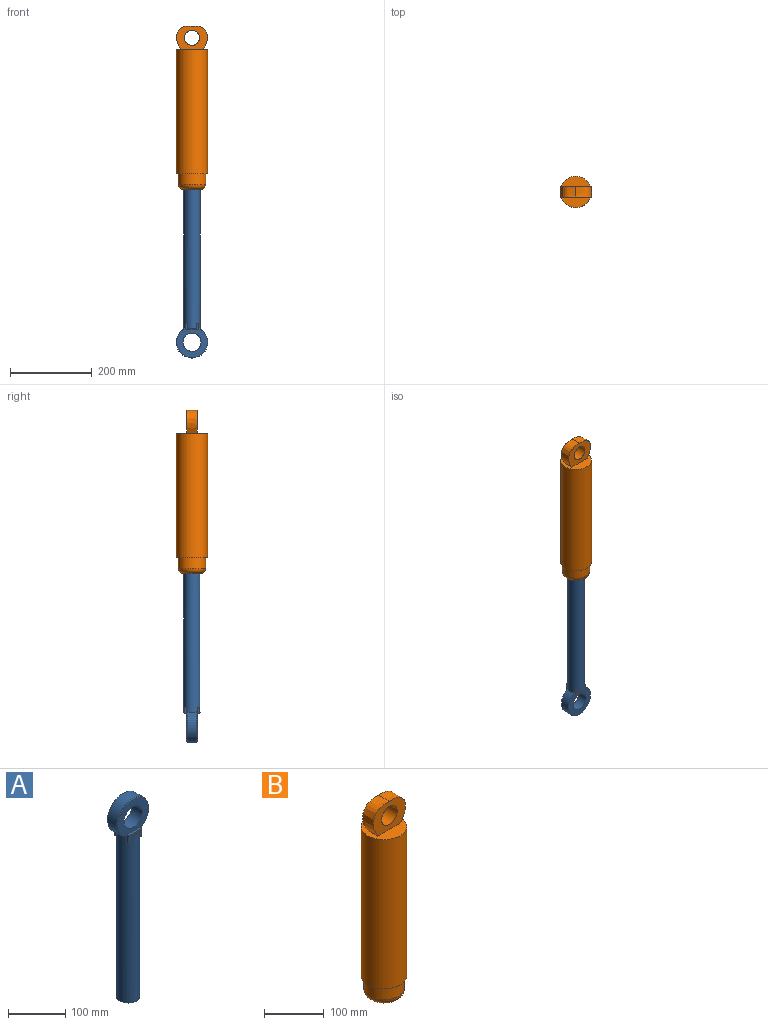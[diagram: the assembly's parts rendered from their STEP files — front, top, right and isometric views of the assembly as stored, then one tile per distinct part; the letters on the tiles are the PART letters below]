
ASSEMBLY  parts=2 mates=1
PART A: 24 faces, bbox 77.5x40.6x427.7 mm
  f0: cylinder r=20.32mm len=355.6mm, axis (0,0,-1), area 44958.8mm2, adj f1,f4,f5,f6,f7,f8,f10,f11
  f1: plane 19.87x2.59mm, normal (0,0,1), area 34.8mm2, adj f0,f17
  f2: plane 74.96x71.44mm, normal (0,1,0), area 2660.6mm2, adj f18,f19,f20,f21,f22
  f3: plane 74.96x71.44mm, normal (0,-1,0), area 2660.6mm2, adj f9,f10,f11,f21,f23
  f4: plane 9.02x0.51mm, normal (0,0,1), area 3.1mm2, adj f0,f8
  f5: plane 9.02x0.51mm, normal (0,0,1), area 3.1mm2, adj f0,f8
  f6: plane 19.87x2.59mm, normal (0,0,1), area 34.8mm2, adj f0,f12
  f7: plane 40.64x40.64mm, normal (0,0,-1), area 1297.2mm2, adj f0
  f8: cylinder r=38.75mm len=77.5mm, axis (0,-1,0), area 4654.6mm2, adj f0,f4,f5,f22,f23
  f9: plane 31.72x5.03mm, normal (0,0,1), area 159.5mm2, adj f3,f10,f11,f12
  f10: plane 16.51x5.03mm, normal (1,0,0), area 83mm2, adj f0,f3,f9,f12,f13
  f11: plane 16.51x5.03mm, normal (-1,0,0), area 83mm2, adj f0,f3,f9,f12,f14
  f12: plane 31.72x16.51mm, normal (0,-1,0), area 261.4mm2, adj f0,f6,f9,f10,f11,f13,f14
  f13: plane 5.93x5.03mm, normal (0,0,-1), area 13mm2, adj f0,f10,f12
  f14: plane 5.93x5.03mm, normal (0,0,-1), area 13mm2, adj f0,f11,f12
  f15: plane 5.93x5.03mm, normal (0,0,-1), area 13mm2, adj f0,f17,f19
  f16: plane 5.93x5.03mm, normal (0,0,-1), area 13mm2, adj f0,f17,f18
  f17: plane 31.72x16.51mm, normal (0,1,0), area 261.4mm2, adj f0,f1,f15,f16,f18,f19,f20
  f18: plane 16.51x5.03mm, normal (-1,0,0), area 83mm2, adj f0,f2,f16,f17,f20
  f19: plane 16.51x5.03mm, normal (1,0,0), area 83mm2, adj f0,f2,f15,f17,f20
  f20: plane 31.72x5.03mm, normal (0,0,1), area 159.5mm2, adj f2,f17,f18,f19
  f21: cylinder r=22.23mm len=44.45mm, axis (0,-1,0), area 3547mm2, adj f2,f3
  f22: cone r=37.48mm half-angle=45deg, axis (0,-1,0), area 369.4mm2, adj f0,f2,f8
  f23: cone r=38.75mm half-angle=45deg, axis (0,1,0), area 369.4mm2, adj f0,f3,f8
PART B: 15 faces, bbox 78x76.2x401.8 mm
  f0: plane 63.5x63.5mm, normal (0,0,1), area 1767.5mm2, adj f2,f3
  f1: plane 63.5x63.5mm, normal (0,0,-1), area 3166.9mm2, adj f2
  f2: cylinder r=31.75mm len=298.45mm, axis (0,0,-1), area 59538.1mm2, adj f0,f1
  f3: cylinder r=21.11mm len=42.21mm, axis (0,0,-1), area 5052.4mm2, adj f0,f7
  f4: cylinder r=38.1mm len=304.8mm, axis (0,0,-1), area 72965.9mm2, adj f5,f6
  f5: plane 76.2x76.2mm, normal (0,0,1), area 3181.4mm2, adj f4,f10,f11,f12,f13
  f6: plane 76.2x76.2mm, normal (0,0,-1), area 960.1mm2, adj f4,f8
  f7: plane 42.31x42.31mm, normal (0,0,-1), area 6.3mm2, adj f3,f9
  f8: cylinder r=33.85mm len=67.71mm, axis (0,0,1), area 5402.7mm2, adj f6,f9
  f9: torus R=21.15mm, axis (0,0,-1), area 3664.8mm2, adj f7,f8
  f10: extruded ~57.85x37.87mm, area 2189.3mm2, adj f5,f11,f12,f13
  f11: extruded ~57.85x37.96mm, area 2191.6mm2, adj f5,f10,f12,f13
  f12: plane 77.99x59.28mm, normal (0,1,0), area 2747.9mm2, adj f5,f10,f11,f14
  f13: plane 77.99x59.28mm, normal (0,-1,0), area 2747.9mm2, adj f5,f10,f11,f14
  f14: cylinder r=18.48mm len=36.95mm, axis (0,1,0), area 2948.6mm2, adj f12,f13
PLACE A rot(axis=(1,0,0),180deg) t=(-116.63,-29.54,-43.19)mm
PLACE B t=(-116.63,-29.54,-19.09)mm
MATE slider A.f0 <-> B.f3  axis (0,0,1) through (-116.63,-29.54,-220.99)mm
